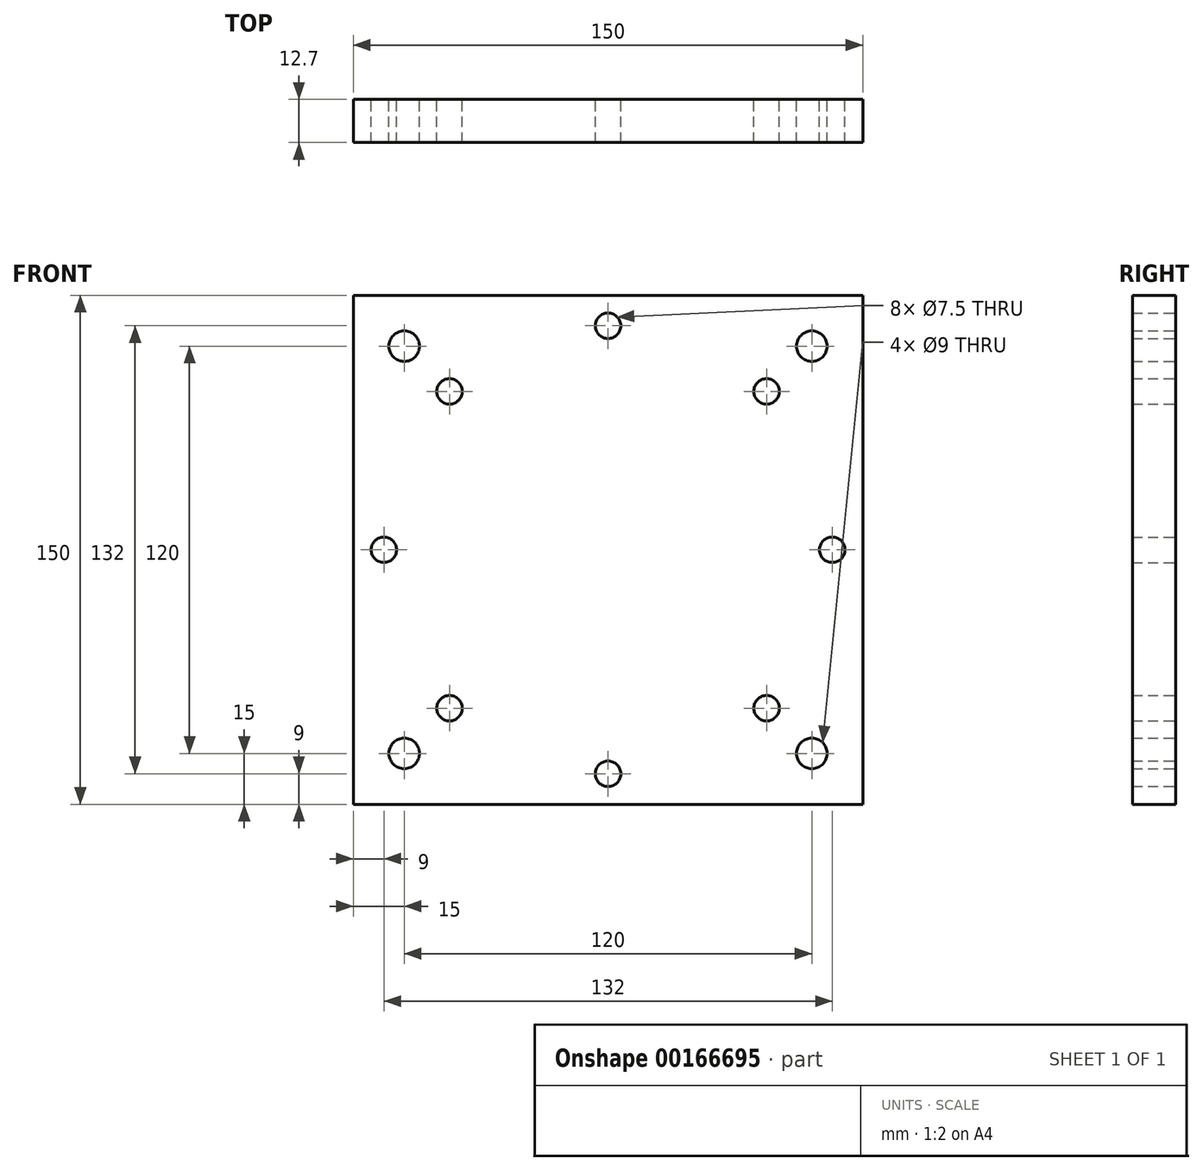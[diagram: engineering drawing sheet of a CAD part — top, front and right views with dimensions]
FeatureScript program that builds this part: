
annotation { "Feature Type Name" : "Feature", "Feature Type Description" : "" }
export const myFeature = defineFeature(function(context is Context, id is Id, definition is map)
    precondition{}
    {
        {
            var Q0;
            Q0=qCreatedBy(makeId("Front.planeOp"),FACE);
            var sketch = newSketch(context, id + "F0", { "sketchPlane" : qUnion([Q0])});
            skLineSegment(sketch, "E0.bottom", {"start": v(75, -75) * mm, "end": v(-75, -75) * mm});
            skLineSegment(sketch, "E0.top", {"start": v(75, 75) * mm, "end": v(-75, 75) * mm});
            skLineSegment(sketch, "E0.left", {"start": v(75, -75) * mm, "end": v(75, 75) * mm});
            skLineSegment(sketch, "E0.right", {"start": v(-75, -75) * mm, "end": v(-75, 75) * mm});
            skPoint(sketch, "E0.middle", {"position": v(0, 0) * mm});
            skSolve(sketch);
        }
        {
            var Q0;
            Q0=makeQuery(id+"F0.imprint","IMPRINT",FACE,{"disambiguationData":[TD([[makeQuery(id+"F0.imprint","IMPRINT",EDGE,{"derivedFrom":sQuery(id+"F0.wireOp",EDGE,"E0.bottom")}),-1.0]])]});
            extrude(context, id + "F1", {"entities" : qUnion([Q0]), "depth" : 12.7 * mm});
        }
        {
            var Q0;
            Q0=qCreatedBy(makeId("Front.planeOp"),FACE);
            var sketch = newSketch(context, id + "F2", { "sketchPlane" : qUnion([Q0])});
            skCircle(sketch, "E1", {"center": v(-60, 60) * mm, "radius": 4.5 * mm});
            skCircle(sketch, "E2", {"center": v(60, 60) * mm, "radius": 4.5 * mm});
            skCircle(sketch, "E3", {"center": v(-60, -60) * mm, "radius": 4.5 * mm});
            skCircle(sketch, "E4", {"center": v(60, -60) * mm, "radius": 4.5 * mm});
            skCircle(sketch, "E5", {"center": v(0, 66) * mm, "radius": 3.75 * mm});
            skCircle(sketch, "E6.1.0", {"center": v(-46.67, 46.67) * mm, "radius": 3.75 * mm});
            skCircle(sketch, "E6.2.0", {"center": v(-66, 0) * mm, "radius": 3.75 * mm});
            skCircle(sketch, "E6.3.0", {"center": v(-46.67, -46.67) * mm, "radius": 3.75 * mm});
            skCircle(sketch, "E6.4.0", {"center": v(0, -66) * mm, "radius": 3.75 * mm});
            skCircle(sketch, "E6.5.0", {"center": v(46.67, -46.67) * mm, "radius": 3.75 * mm});
            skCircle(sketch, "E6.6.0", {"center": v(66, 0) * mm, "radius": 3.75 * mm});
            skCircle(sketch, "E6.7.0", {"center": v(46.67, 46.67) * mm, "radius": 3.75 * mm});
            skPoint(sketch, "E6.center", {"position": v(0, 0) * mm});
            skSolve(sketch);
        }
        {
            var Q0;
            Q0 = qSketchRegion(id + "F2", true);
            extrude(context, id + "F3", {"entities" : qUnion([Q0]), "operationType" : NewBodyOperationType.REMOVE, "endBound" : BoundingType.THROUGH_ALL, "depth" : 25 * mm});
        }
    });
